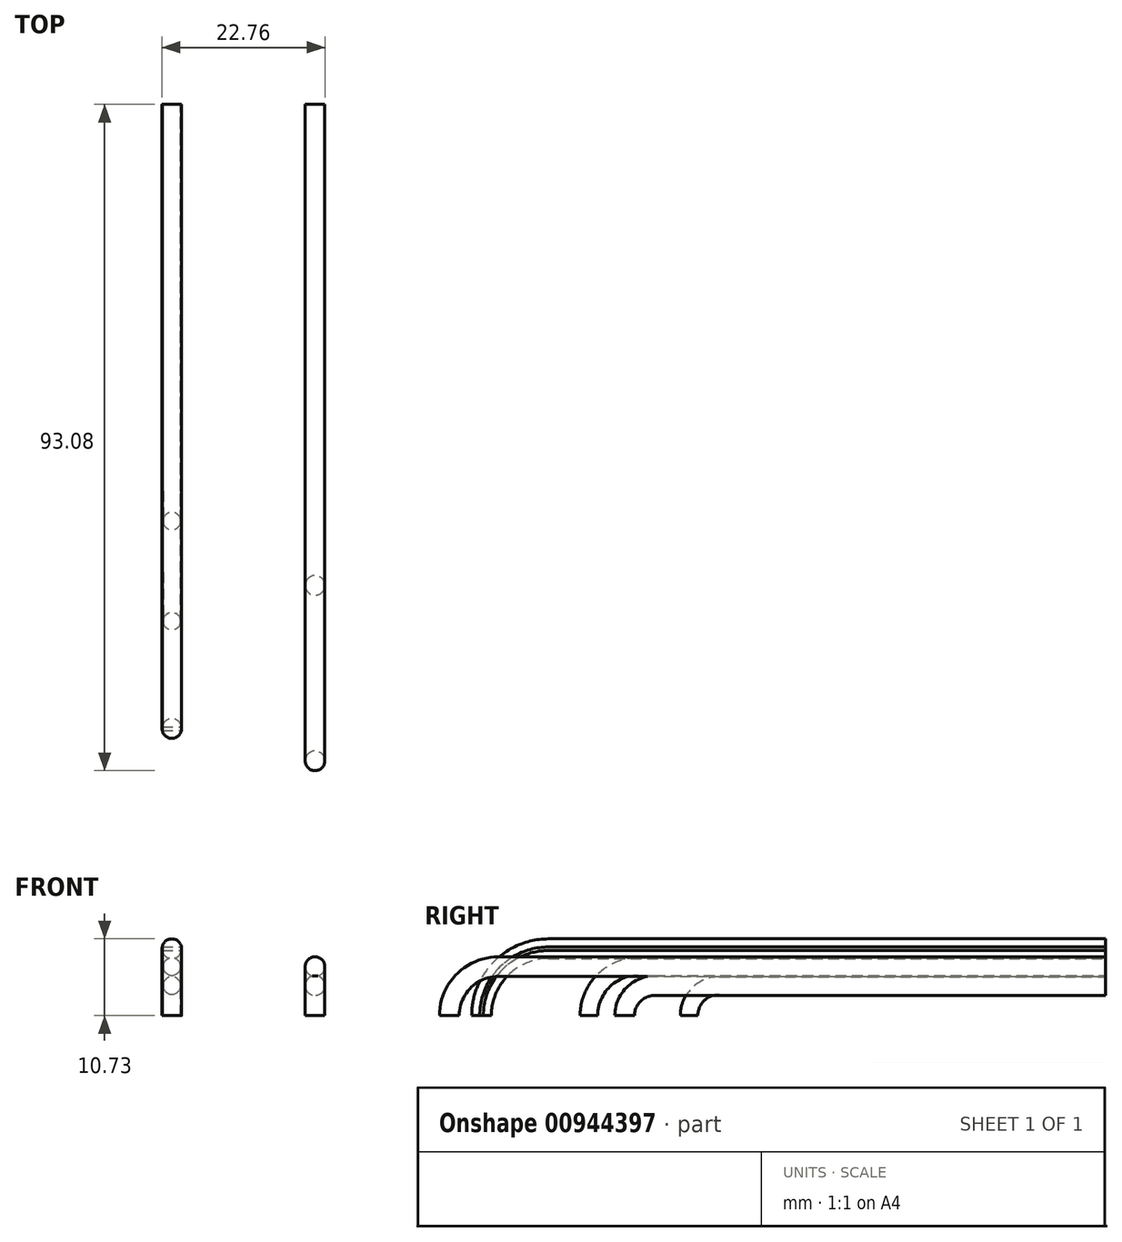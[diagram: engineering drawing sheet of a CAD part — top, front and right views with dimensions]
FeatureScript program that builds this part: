
annotation { "Feature Type Name" : "Feature", "Feature Type Description" : "" }
export const myFeature = defineFeature(function(context is Context, id is Id, definition is map)
    precondition{}
    {
        {
            var Q0;
            Q0=qCreatedBy(makeId("Top.planeOp"),FACE);
            var sketch = newSketch(context, id + "F0", { "sketchPlane" : qUnion([Q0])});
            skLineSegment(sketch, "E0", {"start": v(-10, 76.24) * mm, "end": v(-10, -5.09) * mm, "construction": true});
            skLineSegment(sketch, "E1", {"start": v(10, 71.77) * mm, "end": v(10, -10.19) * mm, "construction": true});
            skCircle(sketch, "E2", {"center": v(-10, 23) * mm, "radius": 1.38 * mm});
            skCircle(sketch, "E3", {"center": v(-10, 29) * mm, "radius": 1.38 * mm});
            skCircle(sketch, "E4", {"center": v(10, 18.5) * mm, "radius": 1.38 * mm});
            skCircle(sketch, "E5", {"center": v(10, 24.5) * mm, "radius": 1.38 * mm});
            skLineSegment(sketch, "E6", {"start": v(-11.35, 23.25) * mm, "end": v(-8.65, 23.25) * mm});
            skLineSegment(sketch, "E7", {"start": v(-11.35, 22.75) * mm, "end": v(-8.65, 22.75) * mm});
            skLineSegment(sketch, "E8", {"start": v(-11.35, 29.25) * mm, "end": v(-8.65, 29.25) * mm});
            skLineSegment(sketch, "E9", {"start": v(-11.35, 28.75) * mm, "end": v(-8.65, 28.75) * mm});
            skCircle(sketch, "E10", {"center": v(-10, 58) * mm, "radius": 1.23 * mm});
            skCircle(sketch, "E11", {"center": v(-10, 44) * mm, "radius": 1.23 * mm});
            skCircle(sketch, "E12", {"center": v(10, 55) * mm, "radius": 1.23 * mm});
            skCircle(sketch, "E13", {"center": v(10, 49) * mm, "radius": 1.38 * mm});
            skSolve(sketch);
        }
        {
            var Q0;
            Q0=qCreatedBy(makeId("Right.planeOp"),FACE);
            cPlane(context, id + "F1", {"entities" : qUnion([Q0]), "cplaneType" : CPlaneType.OFFSET, "offset" : 10 * mm, "oppositeDirection" : true, "width" : 150 * mm, "height" : 150 * mm});
        }
        {
            var Q0;
            Q0=qCreatedBy(makeId("Right.planeOp"),FACE);
            cPlane(context, id + "F2", {"entities" : qUnion([Q0]), "cplaneType" : CPlaneType.OFFSET, "offset" : 10 * mm, "width" : 150 * mm, "height" : 150 * mm});
        }
        {
            var Q0;
            Q0=qCreatedBy(id+"F1.planeOp",FACE);
            var sketch = newSketch(context, id + "F3", { "sketchPlane" : qUnion([Q0])});
            skArc(sketch, "E14", {"start": v(38.35, 9.35) * mm, "mid": v(31.74, 6.61) * mm, "end": v(29, 0) * mm});
            skLineSegment(sketch, "E15", {"start": v(38.35, 9.35) * mm, "end": v(116.2, 9.35) * mm});
            skArc(sketch, "E16", {"start": v(50.85, 6.85) * mm, "mid": v(46, 4.84) * mm, "end": v(44, 0) * mm});
            skLineSegment(sketch, "E17", {"start": v(50.85, 6.85) * mm, "end": v(116.2, 6.85) * mm});
            skArc(sketch, "E18", {"start": v(62.2, 4.2) * mm, "mid": v(59.23, 2.97) * mm, "end": v(58, 0) * mm});
            skLineSegment(sketch, "E19", {"start": v(62.2, 4.2) * mm, "end": v(116.2, 4.2) * mm});
            skSolve(sketch);
        }
        {
            var Q0;
            Q0=qCreatedBy(id+"F2.planeOp",FACE);
            var sketch = newSketch(context, id + "F4", { "sketchPlane" : qUnion([Q0])});
            skArc(sketch, "E20", {"start": v(31.35, 6.85) * mm, "mid": v(26.5, 4.84) * mm, "end": v(24.5, 0) * mm});
            skLineSegment(sketch, "E21", {"start": v(31.35, 6.85) * mm, "end": v(116.2, 6.85) * mm});
            skArc(sketch, "E22", {"start": v(53.2, 4.2) * mm, "mid": v(50.23, 2.97) * mm, "end": v(49, 0) * mm});
            skLineSegment(sketch, "E23", {"start": v(53.2, 4.2) * mm, "end": v(116.2, 4.2) * mm});
            skSolve(sketch);
        }
        {
            var Q0;
            Q0=makeQuery(id+"F0.imprint","IMPRINT",FACE,{"disambiguationData":[TD([[makeQuery(id+"F0.imprint","IMPRINT",EDGE,{"derivedFrom":sQuery(id+"F0.wireOp",EDGE,"E11")}),1.0]])]});
            var Q1;
            Q1=sQuery(id+"F3.wireOp",EDGE,"E16");
            var Q2;
            Q2=sQuery(id+"F3.wireOp",EDGE,"E17");
            sweep(context, id + "F5", {"profiles" : qUnion([Q0]), "path" : qUnion([Q1, Q2])});
        }
        {
            var Q0;
            Q0=makeQuery(id+"F0.imprint","IMPRINT",FACE,{"disambiguationData":[TD([[makeQuery(id+"F0.imprint","IMPRINT",EDGE,{"derivedFrom":sQuery(id+"F0.wireOp",EDGE,"E10")}),1.0]])]});
            var Q1;
            Q1=sQuery(id+"F0.wireOp",EDGE,"ZZW9ILuc-Qh0Z-cEP5-6Sod-cu6Z1KOUDuxO");
            var Q2;
            Q2=sQuery(id+"F3.wireOp",EDGE,"E18");
            var Q3;
            Q3=sQuery(id+"F3.wireOp",EDGE,"E19");
            sweep(context, id + "F6", {"profiles" : qUnion([Q0]), "surfaceProfiles" : qUnion([Q1]), "path" : qUnion([Q2, Q3])});
        }
        {
            var Q0;
            Q0=makeQuery(id+"F0.imprint","IMPRINT",FACE,{"disambiguationData":[TD([[makeQuery(id+"F0.imprint","IMPRINT",EDGE,{"derivedFrom":sQuery(id+"F0.wireOp",EDGE,"E13")}),1.0]])]});
            var Q1;
            Q1=sQuery(id+"F4.wireOp",EDGE,"E23");
            var Q2;
            Q2=sQuery(id+"F4.wireOp",EDGE,"E22");
            sweep(context, id + "F7", {"profiles" : qUnion([Q0]), "path" : qUnion([Q1, Q2])});
        }
        {
            var Q0;
            {var subQ0=sQuery(id+"F0.wireOp",EDGE,"E8");Q0=makeQuery(id+"F0.imprint","IMPRINT",FACE,{"disambiguationData":[TD([[makeQuery(id+"F0.imprint","IMPRINT",EDGE,{"derivedFrom":subQ0}),-1.0]])]});}
            var Q1;
            Q1=sQuery(id+"F3.wireOp",EDGE,"E14");
            var Q2;
            Q2=sQuery(id+"F3.wireOp",EDGE,"E15");
            sweep(context, id + "F8", {"profiles" : qUnion([Q0]), "path" : qUnion([Q1, Q2])});
        }
        {
            var Q0;
            Q0=makeQuery(id+"F0.imprint","IMPRINT",FACE,{"disambiguationData":[TD([[makeQuery(id+"F0.imprint","IMPRINT",EDGE,{"derivedFrom":sQuery(id+"F0.wireOp",EDGE,"E5")}),1.0]])]});
            var Q1;
            Q1=sQuery(id+"F4.wireOp",EDGE,"E21");
            var Q2;
            Q2=sQuery(id+"F4.wireOp",EDGE,"E20");
            sweep(context, id + "F9", {"profiles" : qUnion([Q0]), "path" : qUnion([Q1, Q2])});
        }
        {
            var Q0;
            {var subQ0=sQuery(id+"F0.wireOp",EDGE,"E8");Q0=makeQuery(id+"F0.imprint","IMPRINT",FACE,{"disambiguationData":[TD([[makeQuery(id+"F0.imprint","IMPRINT",EDGE,{"derivedFrom":subQ0}),1.0]])]});}
            var Q1;
            Q1=sQuery(id+"F3.wireOp",EDGE,"E14");
            var Q2;
            Q2=sQuery(id+"F3.wireOp",EDGE,"E15");
            sweep(context, id + "F10", {"profiles" : qUnion([Q0]), "path" : qUnion([Q1, Q2])});
        }
        {
            var Q0;
            {var subQ0=sQuery(id+"F0.wireOp",EDGE,"E9");Q0=makeQuery(id+"F0.imprint","IMPRINT",FACE,{"disambiguationData":[TD([[makeQuery(id+"F0.imprint","IMPRINT",EDGE,{"derivedFrom":subQ0}),-1.0]])]});}
            var Q1;
            Q1=sQuery(id+"F3.wireOp",EDGE,"E14");
            var Q2;
            Q2=sQuery(id+"F3.wireOp",EDGE,"E15");
            sweep(context, id + "F11", {"profiles" : qUnion([Q0]), "path" : qUnion([Q1, Q2])});
        }
    });
